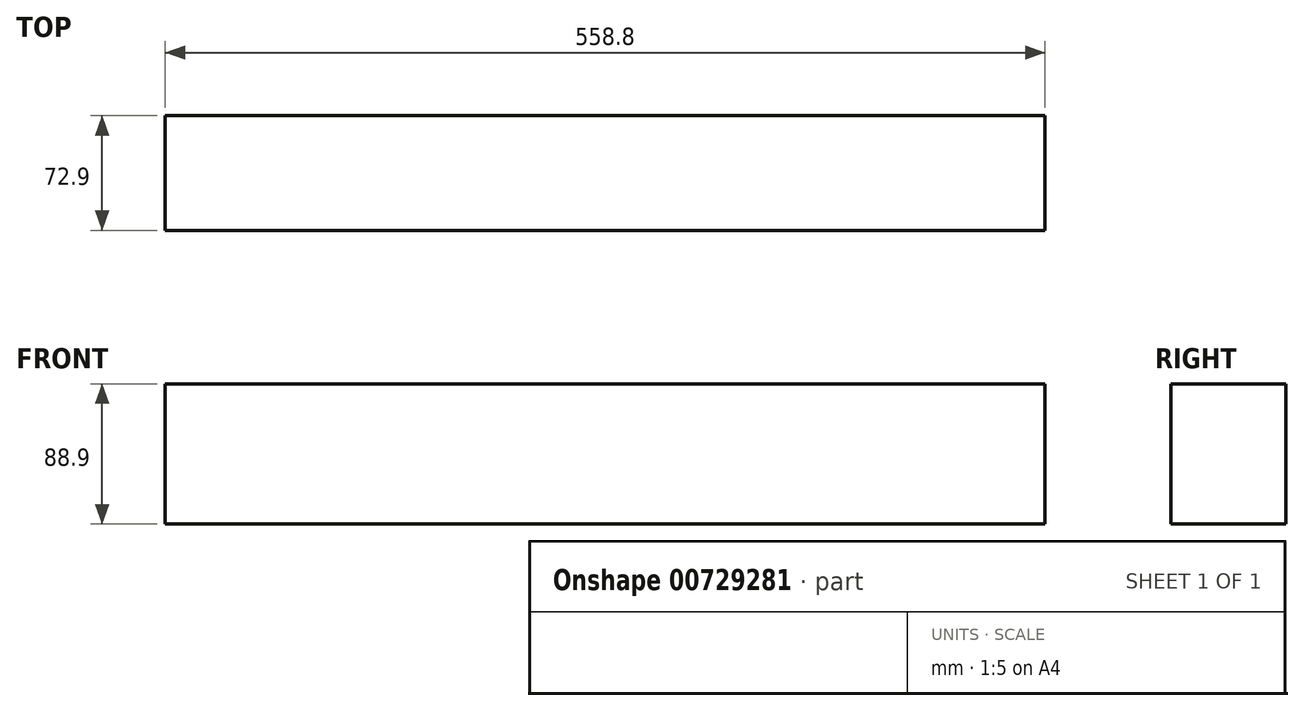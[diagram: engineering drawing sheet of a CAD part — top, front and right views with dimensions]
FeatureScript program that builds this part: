
annotation { "Feature Type Name" : "Feature", "Feature Type Description" : "" }
export const myFeature = defineFeature(function(context is Context, id is Id, definition is map)
    precondition{}
    {
        {
            var Q0;
            Q0=qCreatedBy(makeId("Front.planeOp"),FACE);
            var sketch = newSketch(context, id + "F0", { "sketchPlane" : qUnion([Q0])});
            skLineSegment(sketch, "E0.bottom", {"start": v(-155, 88.9) * mm, "end": v(403.8, 88.9) * mm});
            skLineSegment(sketch, "E0.top", {"start": v(-155, 0) * mm, "end": v(403.8, 0) * mm});
            skLineSegment(sketch, "E0.left", {"start": v(-155, 88.9) * mm, "end": v(-155, 0) * mm});
            skLineSegment(sketch, "E0.right", {"start": v(403.8, 88.9) * mm, "end": v(403.8, 0) * mm});
            skSolve(sketch);
        }
        {
            var Q0;
            Q0=sQuery(id+"F0.wireOp",EDGE,"E0.top");
            var Q1;
            Q1=sQuery(id+"F0.wireOp",EDGE,"E0.left");
            var Q2;
            Q2=sQuery(id+"F0.wireOp",EDGE,"E0.bottom");
            var Q3;
            Q3=sQuery(id+"F0.wireOp",EDGE,"E0.right");
            extrude(context, id + "F1", {"bodyType" : ToolBodyType.SURFACE, "surfaceEntities" : qUnion([Q0, Q1, Q2, Q3]), "depth" : 72.9 * mm, "offsetDistance" : 25.4 * mm});
        }
    });
